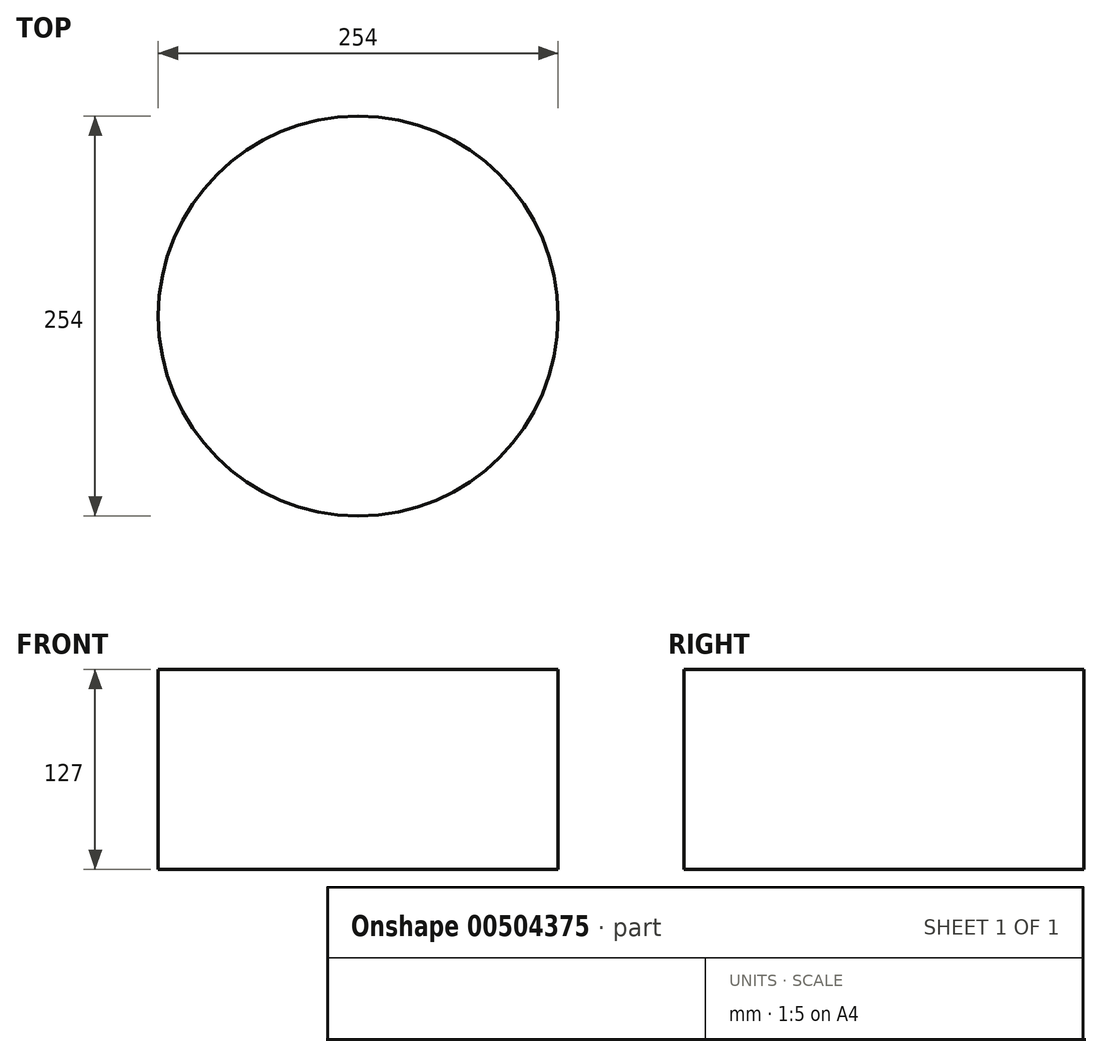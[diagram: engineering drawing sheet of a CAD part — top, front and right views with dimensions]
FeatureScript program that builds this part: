
annotation { "Feature Type Name" : "Feature", "Feature Type Description" : "" }
export const myFeature = defineFeature(function(context is Context, id is Id, definition is map)
    precondition{}
    {
        {
            var Q0;
            Q0=qCreatedBy(makeId("Front.planeOp"),FACE);
            var sketch = newSketch(context, id + "F0", { "sketchPlane" : qUnion([Q0])});
            skLineSegment(sketch, "E0.bottom", {"start": v(-150.45, 83.04) * mm, "end": v(-23.45, 83.04) * mm});
            skLineSegment(sketch, "E0.top", {"start": v(-150.45, -43.96) * mm, "end": v(-23.45, -43.96) * mm});
            skLineSegment(sketch, "E0.left", {"start": v(-150.45, 83.04) * mm, "end": v(-150.45, -43.96) * mm});
            skLineSegment(sketch, "E0.right", {"start": v(-23.45, 83.04) * mm, "end": v(-23.45, -43.96) * mm});
            skSolve(sketch);
        }
        {
            var Q0;
            Q0=makeQuery(id+"F0.imprint","IMPRINT",FACE,{"disambiguationData":[TD([[makeQuery(id+"F0.imprint","IMPRINT",EDGE,{"derivedFrom":sQuery(id+"F0.wireOp",EDGE,"E0.bottom")}),-1.0]])]});
            var Q1;
            Q1=sQuery(id+"F0.wireOp",EDGE,"E0.right");
            revolve(context, id + "F1", {"entities" : qUnion([Q0]), "axis" : qUnion([Q1]), "revolveType" : RevolveType.FULL});
        }
    });
